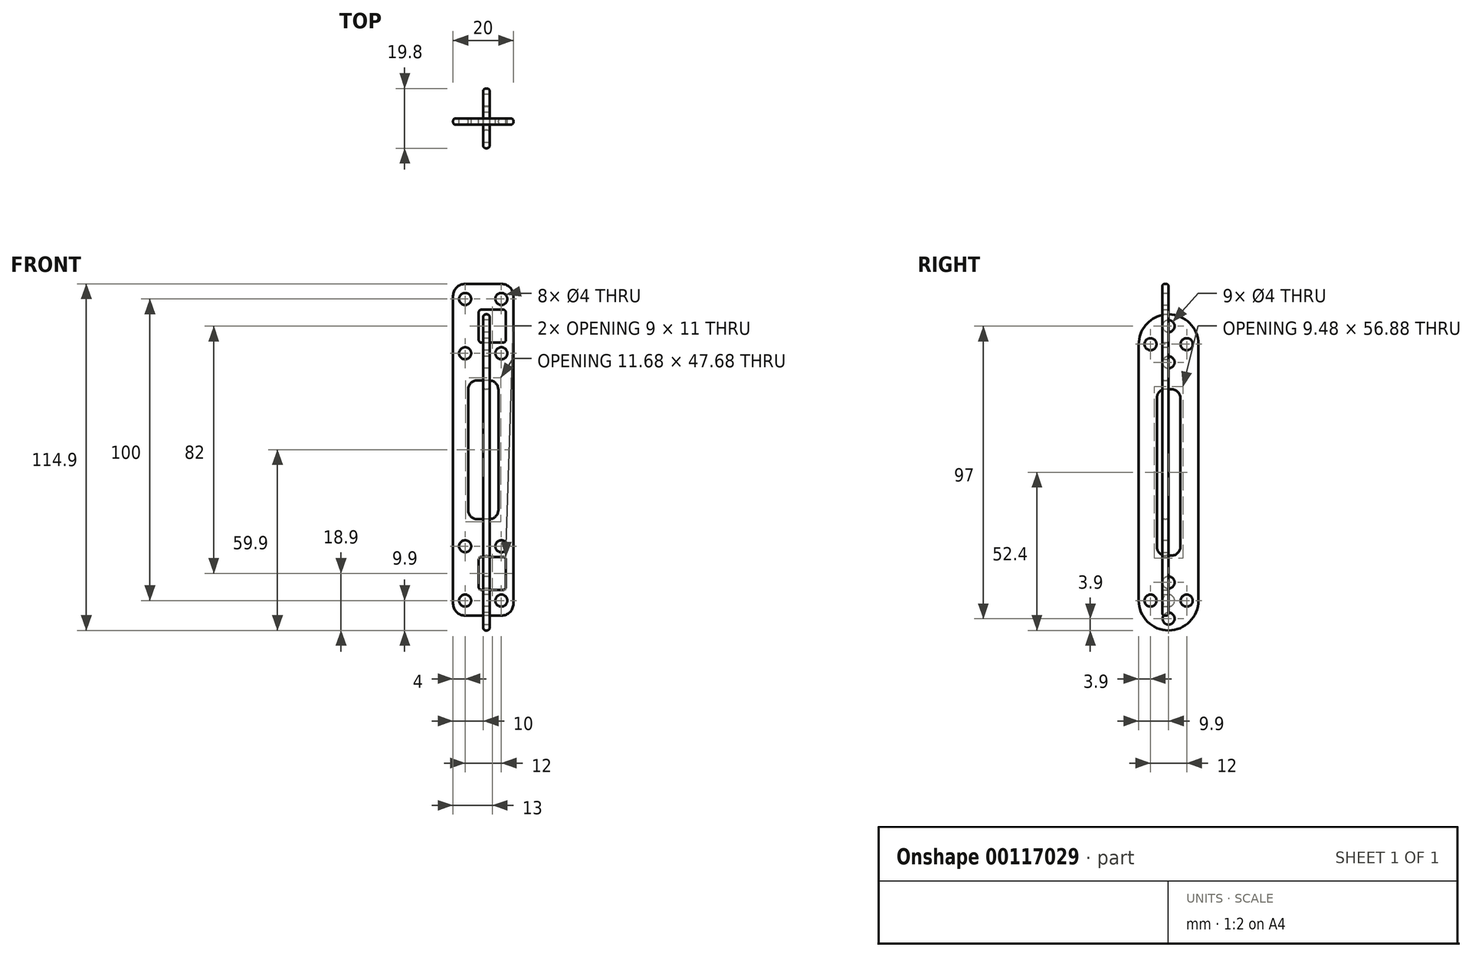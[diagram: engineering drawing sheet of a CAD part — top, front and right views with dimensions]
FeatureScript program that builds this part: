
annotation { "Feature Type Name" : "Feature", "Feature Type Description" : "" }
export const myFeature = defineFeature(function(context is Context, id is Id, definition is map)
    precondition{}
    {
        {
            assignVariable(context, id + "F0", {"name" : "tolerance", "anyValue" : 0.1});
        }
        {
            assignVariable(context, id + "F1", {"name" : "thickness", "anyValue" : 2.2 - getVariable(context, 'tolerance')});
        }
        {
            var Q0;
            Q0=qCreatedBy(makeId("Right.planeOp"),FACE);
            var sketch = newSketch(context, id + "F2", { "sketchPlane" : qUnion([Q0])});
            skLineSegment(sketch, "E0.rect.bottom", {"start": v(12, -9) * mm, "end": v(-12, -9) * mm});
            skLineSegment(sketch, "E0.rect.top", {"start": v(12, 27) * mm, "end": v(-12, 27) * mm});
            skLineSegment(sketch, "E0.rect.left", {"start": v(12, -9) * mm, "end": v(12, 27) * mm});
            skLineSegment(sketch, "E0.rect.right", {"start": v(-12, -9) * mm, "end": v(-12, 27) * mm});
            skPoint(sketch, "E0.rect.middle", {"position": v(0, 9) * mm});
            skCircle(sketch, "E1", {"center": v(0, 0) * mm, "radius": 8.9 * mm});
            skLineSegment(sketch, "E2", {"start": v(0, 27) * mm, "end": v(0, -9) * mm, "construction": true});
            skCircle(sketch, "E3", {"center": v(0, 0) * mm, "radius": 6 * mm, "construction": true});
            skCircle(sketch, "E4", {"center": v(0, -6) * mm, "radius": 2 * mm});
            skCircle(sketch, "E5.1.0", {"center": v(6, 0) * mm, "radius": 2 * mm});
            skCircle(sketch, "E5.2.0", {"center": v(0, 6) * mm, "radius": 2 * mm});
            skCircle(sketch, "E5.3.0", {"center": v(-6, 0) * mm, "radius": 2 * mm});
            skCircle(sketch, "E6", {"center": v(-4.24, 4.24) * mm, "radius": 0.8 * mm});
            skCircle(sketch, "E7.1.0", {"center": v(-4.24, -4.24) * mm, "radius": 0.8 * mm});
            skCircle(sketch, "E7.2.0", {"center": v(4.24, -4.24) * mm, "radius": 0.8 * mm});
            skCircle(sketch, "E7.3.0", {"center": v(4.24, 4.24) * mm, "radius": 0.8 * mm});
            skLineSegment(sketch, "E8", {"start": v(-6, 24) * mm, "end": v(6, 24) * mm, "construction": true});
            skCircle(sketch, "E9", {"center": v(-6, 24) * mm, "radius": 2 * mm});
            skCircle(sketch, "E10", {"center": v(0, 24) * mm, "radius": 2 * mm});
            skCircle(sketch, "E11", {"center": v(6, 24) * mm, "radius": 2 * mm});
            skPoint(sketch, "E12.center", {"position": v(0, 100) * mm});
            skLineSegment(sketch, "E13.rect.right", {"start": v(12, 109) * mm, "end": v(12, 73) * mm});
            skCircle(sketch, "E14", {"center": v(-6, 76) * mm, "radius": 2 * mm});
            skLineSegment(sketch, "E15", {"start": v(0, 73) * mm, "end": v(0, 109) * mm, "construction": true});
            skCircle(sketch, "E16", {"center": v(0, 100) * mm, "radius": 8.9 * mm});
            skLineSegment(sketch, "E13.rect.left", {"start": v(-12, 109) * mm, "end": v(-12, 73) * mm});
            skLineSegment(sketch, "E13.rect.bottom", {"start": v(-12, 109) * mm, "end": v(12, 109) * mm});
            skLineSegment(sketch, "E13.rect.top", {"start": v(-12, 73) * mm, "end": v(12, 73) * mm});
            skLineSegment(sketch, "E17", {"start": v(6, 76) * mm, "end": v(-6, 76) * mm, "construction": true});
            skCircle(sketch, "E18", {"center": v(0, 76) * mm, "radius": 2 * mm});
            skPoint(sketch, "E13.rect.middle", {"position": v(0, 91) * mm});
            skCircle(sketch, "E12.2.0", {"center": v(0, 94) * mm, "radius": 2 * mm});
            skCircle(sketch, "E12.1.0", {"center": v(-6, 100) * mm, "radius": 2 * mm});
            skCircle(sketch, "E19", {"center": v(0, 100) * mm, "radius": 6 * mm, "construction": true});
            skCircle(sketch, "E20", {"center": v(0, 106) * mm, "radius": 2 * mm});
            skCircle(sketch, "E21", {"center": v(-4.24, 104.24) * mm, "radius": 0.8 * mm});
            skCircle(sketch, "E12.3.0", {"center": v(6, 100) * mm, "radius": 2 * mm});
            skCircle(sketch, "E22.3.0", {"center": v(4.24, 104.24) * mm, "radius": 0.8 * mm});
            skCircle(sketch, "E22.2.0", {"center": v(4.24, 95.76) * mm, "radius": 0.8 * mm});
            skCircle(sketch, "E22.1.0", {"center": v(-4.24, 95.76) * mm, "radius": 0.8 * mm});
            skCircle(sketch, "E23", {"center": v(6, 76) * mm, "radius": 2 * mm});
            skSolve(sketch);
        }
        {
            var Q0;
            Q0=qCreatedBy(makeId("Front.planeOp"),FACE);
            var sketch = newSketch(context, id + "F3", { "sketchPlane" : qUnion([Q0])});
            skLineSegment(sketch, "E24", {"start": v(0, 22.5) * mm, "end": v(9, 22.5) * mm});
            skLineSegment(sketch, "E25", {"start": v(9, 22.5) * mm, "end": v(9, 27) * mm});
            skLineSegment(sketch, "E26", {"start": v(9, 27) * mm, "end": v(12, 27) * mm});
            skLineSegment(sketch, "E27", {"start": v(12, 27) * mm, "end": v(12, -9) * mm});
            skLineSegment(sketch, "E28", {"start": v(12, -9) * mm, "end": v(0, -9) * mm});
            skLineSegment(sketch, "E29", {"start": v(12, 8.9) * mm, "end": v(15, 8.9) * mm});
            skLineSegment(sketch, "E30", {"start": v(15, 8.9) * mm, "end": v(15, -8.9) * mm});
            skLineSegment(sketch, "E31", {"start": v(15, -8.9) * mm, "end": v(12, -8.9) * mm});
            skLineSegment(sketch, "E32", {"start": v(0, 1.45) * mm, "end": v(0, -56.88) * mm, "construction": true});
            skLineSegment(sketch, "E33", {"start": v(0, 0) * mm, "end": v(15, 0) * mm, "construction": true});
            skLineSegment(sketch, "E34.MirrorCS", {"start": v(-15, 8.9) * mm, "end": v(-15, -8.9) * mm});
            skLineSegment(sketch, "E35.MirrorCS", {"start": v(0, 22.5) * mm, "end": v(-9, 22.5) * mm});
            skLineSegment(sketch, "E36.MirrorCS", {"start": v(0, 0) * mm, "end": v(-15, 0) * mm, "construction": true});
            skLineSegment(sketch, "E37.MirrorCS", {"start": v(-9, 22.5) * mm, "end": v(-9, 27) * mm});
            skLineSegment(sketch, "E38.MirrorCS", {"start": v(-12, 8.9) * mm, "end": v(-15, 8.9) * mm});
            skLineSegment(sketch, "E39.MirrorCS", {"start": v(-12, -9) * mm, "end": v(0, -9) * mm});
            skLineSegment(sketch, "E40.MirrorCS", {"start": v(-12, 27) * mm, "end": v(-12, -9) * mm});
            skLineSegment(sketch, "E41.MirrorCS", {"start": v(-15, -8.9) * mm, "end": v(-12, -8.9) * mm});
            skLineSegment(sketch, "E42.MirrorCS", {"start": v(-9, 27) * mm, "end": v(-12, 27) * mm});
            skLineSegment(sketch, "E43.MirrorCS", {"start": v(0, 100) * mm, "end": v(-15, 100) * mm, "construction": true});
            skLineSegment(sketch, "E44.MirrorCS", {"start": v(0, 77.5) * mm, "end": v(-9, 77.5) * mm});
            skLineSegment(sketch, "E45", {"start": v(15, 108.9) * mm, "end": v(15, 91.1) * mm});
            skLineSegment(sketch, "E46.MirrorCS", {"start": v(-15, 108.9) * mm, "end": v(-15, 91.1) * mm});
            skLineSegment(sketch, "E47", {"start": v(0, 57.8) * mm, "end": v(0, 0) * mm, "construction": true});
            skLineSegment(sketch, "E48", {"start": v(12, 109) * mm, "end": v(0, 109) * mm});
            skLineSegment(sketch, "E49", {"start": v(12, 109) * mm, "end": v(12, 73) * mm});
            skLineSegment(sketch, "E50", {"start": v(0, 77.5) * mm, "end": v(9, 77.5) * mm});
            skLineSegment(sketch, "E51.MirrorCS", {"start": v(-12, 109) * mm, "end": v(0, 109) * mm});
            skLineSegment(sketch, "E52.MirrorCS", {"start": v(-12, 109) * mm, "end": v(-12, 73) * mm});
            skLineSegment(sketch, "E53", {"start": v(0, 100) * mm, "end": v(15, 100) * mm, "construction": true});
            skLineSegment(sketch, "E54", {"start": v(12, 108.9) * mm, "end": v(15, 108.9) * mm});
            skLineSegment(sketch, "E55", {"start": v(9, 73) * mm, "end": v(12, 73) * mm});
            skLineSegment(sketch, "E56", {"start": v(9, 73) * mm, "end": v(9, 77.5) * mm});
            skLineSegment(sketch, "E57.MirrorCS", {"start": v(-9, 73) * mm, "end": v(-12, 73) * mm});
            skLineSegment(sketch, "E58.MirrorCS", {"start": v(-12, 108.9) * mm, "end": v(-15, 108.9) * mm});
            skLineSegment(sketch, "E59.MirrorCS", {"start": v(-9, 73) * mm, "end": v(-9, 77.5) * mm});
            skLineSegment(sketch, "E60.MirrorCS", {"start": v(-15, 91.1) * mm, "end": v(-12, 91.1) * mm});
            skLineSegment(sketch, "E61", {"start": v(15, 91.1) * mm, "end": v(12, 91.1) * mm});
            skLineSegment(sketch, "E62.bottom", {"start": v(-6, 18) * mm, "end": v(6, 18) * mm, "construction": true});
            skLineSegment(sketch, "E62.top", {"start": v(-6, 0) * mm, "end": v(6, 0) * mm, "construction": true});
            skLineSegment(sketch, "E62.left", {"start": v(-6, 18) * mm, "end": v(-6, 0) * mm, "construction": true});
            skLineSegment(sketch, "E62.right", {"start": v(6, 18) * mm, "end": v(6, 0) * mm, "construction": true});
            skCircle(sketch, "E63", {"center": v(6, 0) * mm, "radius": 2 * mm});
            skCircle(sketch, "E64", {"center": v(-6, 0) * mm, "radius": 2 * mm});
            skCircle(sketch, "E65", {"center": v(-6, 18) * mm, "radius": 2 * mm});
            skCircle(sketch, "E66", {"center": v(6, 18) * mm, "radius": 2 * mm});
            skLineSegment(sketch, "E67.left", {"start": v(-6, 100) * mm, "end": v(-6, 82) * mm, "construction": true});
            skCircle(sketch, "E68", {"center": v(-6, 100) * mm, "radius": 2 * mm});
            skLineSegment(sketch, "E67.right", {"start": v(6, 100) * mm, "end": v(6, 82) * mm, "construction": true});
            skLineSegment(sketch, "E67.bottom", {"start": v(-6, 100) * mm, "end": v(6, 100) * mm, "construction": true});
            skCircle(sketch, "E69", {"center": v(6, 100) * mm, "radius": 2 * mm});
            skCircle(sketch, "E70", {"center": v(6, 82) * mm, "radius": 2 * mm});
            skLineSegment(sketch, "E67.top", {"start": v(-6, 82) * mm, "end": v(6, 82) * mm, "construction": true});
            skCircle(sketch, "E71", {"center": v(-6, 82) * mm, "radius": 2 * mm});
            skLineSegment(sketch, "E72.rect.bottom", {"start": v(7.5, 96.5) * mm, "end": v(-7.5, 96.5) * mm});
            skLineSegment(sketch, "E72.rect.top", {"start": v(7.5, 85.5) * mm, "end": v(-7.5, 85.5) * mm});
            skLineSegment(sketch, "E72.rect.left", {"start": v(7.5, 96.5) * mm, "end": v(7.5, 85.5) * mm});
            skLineSegment(sketch, "E72.rect.right", {"start": v(-7.5, 96.5) * mm, "end": v(-7.5, 85.5) * mm});
            skPoint(sketch, "E72.rect.middle", {"position": v(0, 91) * mm});
            skLineSegment(sketch, "E73.rect.bottom", {"start": v(7.5, 3.5) * mm, "end": v(-7.5, 3.5) * mm});
            skLineSegment(sketch, "E73.rect.top", {"start": v(7.5, 14.5) * mm, "end": v(-7.5, 14.5) * mm});
            skLineSegment(sketch, "E73.rect.left", {"start": v(7.5, 3.5) * mm, "end": v(7.5, 14.5) * mm});
            skLineSegment(sketch, "E73.rect.right", {"start": v(-7.5, 3.5) * mm, "end": v(-7.5, 14.5) * mm});
            skPoint(sketch, "E73.rect.middle", {"position": v(0, 9) * mm});
            skSolve(sketch);
        }
        {
            var Q0;
            Q0=qCreatedBy(makeId("Front.planeOp"),FACE);
            var sketch = newSketch(context, id + "F4", { "sketchPlane" : qUnion([Q0])});
            skLineSegment(sketch, "E74.rect.bottom", {"start": v(6, 105) * mm, "end": v(-6, 105) * mm});
            skLineSegment(sketch, "E74.rect.top", {"start": v(6, -5) * mm, "end": v(-6, -5) * mm});
            skLineSegment(sketch, "E74.rect.left", {"start": v(10, 101) * mm, "end": v(10, -1) * mm});
            skLineSegment(sketch, "E74.rect.right", {"start": v(-10, 101) * mm, "end": v(-10, -1) * mm});
            skPoint(sketch, "E74.rect.middle", {"position": v(0, 50) * mm});
            skCircle(sketch, "E75", {"center": v(-6, 18) * mm, "radius": 2 * mm});
            skCircle(sketch, "E76", {"center": v(6, 18) * mm, "radius": 2 * mm});
            skCircle(sketch, "E77", {"center": v(-6, 0) * mm, "radius": 2 * mm});
            skCircle(sketch, "E78", {"center": v(6, 0) * mm, "radius": 2 * mm});
            skCircle(sketch, "E79", {"center": v(-6, 82) * mm, "radius": 2 * mm});
            skCircle(sketch, "E80", {"center": v(6, 82) * mm, "radius": 2 * mm});
            skCircle(sketch, "E81", {"center": v(-6, 100) * mm, "radius": 2 * mm});
            skCircle(sketch, "E82", {"center": v(6, 100) * mm, "radius": 2 * mm});
            skPoint(sketch, "E83.visualSharp", {"position": v(-10, 105) * mm});
            skArc(sketch, "E83.filletArc", {"start": v(-6, 105) * mm, "mid": v(-8.83, 103.83) * mm, "end": v(-10, 101) * mm});
            skPoint(sketch, "E84.visualSharp", {"position": v(10, 105) * mm});
            skArc(sketch, "E84.filletArc", {"start": v(10, 101) * mm, "mid": v(8.83, 103.83) * mm, "end": v(6, 105) * mm});
            skPoint(sketch, "E85.visualSharp", {"position": v(10, -5) * mm});
            skArc(sketch, "E85.filletArc", {"start": v(6, -5) * mm, "mid": v(8.83, -3.83) * mm, "end": v(10, -1) * mm});
            skPoint(sketch, "E86.visualSharp", {"position": v(-10, -5) * mm});
            skArc(sketch, "E86.filletArc", {"start": v(-10, -1) * mm, "mid": v(-8.83, -3.83) * mm, "end": v(-6, -5) * mm});
            skLineSegment(sketch, "E87.rect.bottom", {"start": v(2, 27) * mm, "end": v(-2, 27) * mm});
            skLineSegment(sketch, "E87.rect.top", {"start": v(2, 73) * mm, "end": v(-2, 73) * mm});
            skLineSegment(sketch, "E87.rect.left", {"start": v(5, 30) * mm, "end": v(5, 70) * mm});
            skLineSegment(sketch, "E87.rect.right", {"start": v(-5, 30) * mm, "end": v(-5, 70) * mm});
            skPoint(sketch, "E88.visualSharp", {"position": v(-5, 73) * mm});
            skArc(sketch, "E88.filletArc", {"start": v(-2, 73) * mm, "mid": v(-4.12, 72.12) * mm, "end": v(-5, 70) * mm});
            skPoint(sketch, "E89.visualSharp", {"position": v(5, 73) * mm});
            skArc(sketch, "E89.filletArc", {"start": v(5, 70) * mm, "mid": v(4.12, 72.12) * mm, "end": v(2, 73) * mm});
            skPoint(sketch, "E90.visualSharp", {"position": v(5, 27) * mm});
            skArc(sketch, "E90.filletArc", {"start": v(2, 27) * mm, "mid": v(4.12, 27.88) * mm, "end": v(5, 30) * mm});
            skPoint(sketch, "E91.visualSharp", {"position": v(-5, 27) * mm});
            skArc(sketch, "E91.filletArc", {"start": v(-5, 30) * mm, "mid": v(-4.12, 27.88) * mm, "end": v(-2, 27) * mm});
            skSolve(sketch);
        }
        {
            var Q0;
            Q0=makeQuery(id+"F4.imprint","IMPRINT",FACE,{"disambiguationData":[TD([[makeQuery(id+"F4.imprint","IMPRINT",EDGE,{"derivedFrom":sQuery(id+"F4.wireOp",EDGE,"E74.rect.bottom")}),1.0]])]});
            extrude(context, id + "F5", {"entities" : qUnion([Q0]), "depth" : (getVariable(context, 'thickness')) * mm});
        }
        {
            var Q0;
            Q0=qCreatedBy(makeId("Front.planeOp"),FACE);
            var sketch = newSketch(context, id + "F6", { "sketchPlane" : qUnion([Q0])});
            skLineSegment(sketch, "E92.rect.bottom", {"start": v(-0.5, 14.5) * mm, "end": v(6.5, 14.5) * mm});
            skLineSegment(sketch, "E92.rect.top", {"start": v(-0.5, 3.5) * mm, "end": v(6.5, 3.5) * mm});
            skLineSegment(sketch, "E92.rect.left", {"start": v(-1.5, 13.5) * mm, "end": v(-1.5, 4.5) * mm});
            skLineSegment(sketch, "E92.rect.right", {"start": v(7.5, 13.5) * mm, "end": v(7.5, 4.5) * mm});
            skPoint(sketch, "E92.rect.middle", {"position": v(3, 9) * mm});
            skPoint(sketch, "E93.visualSharp", {"position": v(-1.5, 14.5) * mm});
            skArc(sketch, "E93.filletArc", {"start": v(-0.5, 14.5) * mm, "mid": v(-1.2, 14.2) * mm, "end": v(-1.5, 13.5) * mm});
            skPoint(sketch, "E94.visualSharp", {"position": v(7.5, 14.5) * mm});
            skArc(sketch, "E94.filletArc", {"start": v(7.5, 13.5) * mm, "mid": v(7.2, 14.2) * mm, "end": v(6.5, 14.5) * mm});
            skPoint(sketch, "E95.visualSharp", {"position": v(7.5, 3.5) * mm});
            skArc(sketch, "E95.filletArc", {"start": v(6.5, 3.5) * mm, "mid": v(7.2, 3.8) * mm, "end": v(7.5, 4.5) * mm});
            skPoint(sketch, "E96.visualSharp", {"position": v(-1.5, 3.5) * mm});
            skArc(sketch, "E96.filletArc", {"start": v(-1.5, 4.5) * mm, "mid": v(-1.2, 3.8) * mm, "end": v(-0.5, 3.5) * mm});
            skPoint(sketch, "E97.visualSharp", {"position": v(7.5, 96.5) * mm});
            skPoint(sketch, "E98.visualSharp", {"position": v(-1.5, 85.5) * mm});
            skPoint(sketch, "E99.rect.middle", {"position": v(3, 91) * mm});
            skPoint(sketch, "E100.visualSharp", {"position": v(7.5, 85.5) * mm});
            skLineSegment(sketch, "E99.rect.top", {"start": v(-0.5, 85.5) * mm, "end": v(6.5, 85.5) * mm});
            skLineSegment(sketch, "E99.rect.right", {"start": v(7.5, 95.5) * mm, "end": v(7.5, 86.5) * mm});
            skPoint(sketch, "E101.visualSharp", {"position": v(-1.5, 96.5) * mm});
            skLineSegment(sketch, "E99.rect.bottom", {"start": v(-0.5, 96.5) * mm, "end": v(6.5, 96.5) * mm});
            skLineSegment(sketch, "E99.rect.left", {"start": v(-1.5, 95.5) * mm, "end": v(-1.5, 86.5) * mm});
            skArc(sketch, "E98.filletArc", {"start": v(-1.5, 86.5) * mm, "mid": v(-1.2, 85.8) * mm, "end": v(-0.5, 85.5) * mm});
            skArc(sketch, "E101.filletArc", {"start": v(-0.5, 96.5) * mm, "mid": v(-1.2, 96.2) * mm, "end": v(-1.5, 95.5) * mm});
            skArc(sketch, "E97.filletArc", {"start": v(7.5, 95.5) * mm, "mid": v(7.2, 96.2) * mm, "end": v(6.5, 96.5) * mm});
            skArc(sketch, "E100.filletArc", {"start": v(6.5, 85.5) * mm, "mid": v(7.2, 85.8) * mm, "end": v(7.5, 86.5) * mm});
            skSolve(sketch);
        }
        {
            var Q0;
            Q0=qSketchRegion(id+"F6",true);
            extrude(context, id + "F7", {"entities" : qUnion([Q0]), "operationType" : NewBodyOperationType.REMOVE, "endBound" : BoundingType.UP_TO_NEXT, "depth" : 25 * mm});
        }
        {
            var Q0;
            Q0=makeQuery(id+"F5.opExtrude","SWEPT_FACE",FACE,{"disambiguationData":[OSD([sQuery(id+"F4.wireOp",EDGE,"E74.rect.left")])]});
            var Q1;
            Q1=makeQuery(id+"F5.opExtrude","SWEPT_FACE",FACE,{"disambiguationData":[OSD([sQuery(id+"F4.wireOp",EDGE,"E87.rect.right")])]});
            fillet(context, id + "F8", {"entities" : qUnion([Q0, Q1]), "radius" : (getVariable(context, 'thickness') / 2.5) * mm, "tangentPropagation" : true, "allowEdgeOverflow" : false});
        }
        {
            var Q0;
            Q0=qCreatedBy(makeId("Right.planeOp"),FACE);
            var sketch = newSketch(context, id + "F9", { "sketchPlane" : qUnion([Q0])});
            skCircle(sketch, "E102", {"center": v(0, 0) * mm, "radius": 9.9 * mm});
            skLineSegment(sketch, "E103", {"start": v(9.9, 0) * mm, "end": v(9.9, 85) * mm});
            skLineSegment(sketch, "E104", {"start": v(-9.9, 85) * mm, "end": v(-9.9, 0) * mm});
            skCircle(sketch, "E105", {"center": v(-6, 0) * mm, "radius": 2 * mm});
            skCircle(sketch, "E106", {"center": v(0, 6) * mm, "radius": 2 * mm});
            skCircle(sketch, "E107", {"center": v(6, 0) * mm, "radius": 2 * mm});
            skCircle(sketch, "E108", {"center": v(0, -6) * mm, "radius": 2 * mm});
            skCircle(sketch, "E109", {"center": v(0, 0) * mm, "radius": 2 * mm});
            skLineSegment(sketch, "E110.rect.bottom", {"start": v(0.9, 14.9) * mm, "end": v(-0.9, 14.9) * mm});
            skLineSegment(sketch, "E110.rect.top", {"start": v(0.9, 70.1) * mm, "end": v(-0.9, 70.1) * mm});
            skLineSegment(sketch, "E110.rect.left", {"start": v(3.9, 17.9) * mm, "end": v(3.9, 67.1) * mm});
            skLineSegment(sketch, "E110.rect.right", {"start": v(-3.9, 17.9) * mm, "end": v(-3.9, 67.1) * mm});
            skPoint(sketch, "E110.rect.middle", {"position": v(0, 42.5) * mm});
            skPoint(sketch, "E111.visualSharp", {"position": v(-3.9, 14.9) * mm});
            skArc(sketch, "E111.filletArc", {"start": v(-3.9, 17.9) * mm, "mid": v(-3.02, 15.78) * mm, "end": v(-0.9, 14.9) * mm});
            skPoint(sketch, "E112.visualSharp", {"position": v(3.9, 14.9) * mm});
            skArc(sketch, "E112.filletArc", {"start": v(0.9, 14.9) * mm, "mid": v(3.02, 15.78) * mm, "end": v(3.9, 17.9) * mm});
            skPoint(sketch, "E113.visualSharp", {"position": v(-3.9, 70.1) * mm});
            skArc(sketch, "E113.filletArc", {"start": v(-0.9, 70.1) * mm, "mid": v(-3.02, 69.22) * mm, "end": v(-3.9, 67.1) * mm});
            skPoint(sketch, "E114.visualSharp", {"position": v(3.9, 70.1) * mm});
            skArc(sketch, "E114.filletArc", {"start": v(3.9, 67.1) * mm, "mid": v(3.02, 69.22) * mm, "end": v(0.9, 70.1) * mm});
            skCircle(sketch, "E115", {"center": v(0, 85) * mm, "radius": 9.9 * mm});
            skCircle(sketch, "E116", {"center": v(0, 85) * mm, "radius": 6 * mm, "construction": true});
            skCircle(sketch, "E117", {"center": v(0, 91) * mm, "radius": 2 * mm});
            skCircle(sketch, "E118.1.0", {"center": v(-6, 85) * mm, "radius": 2 * mm});
            skCircle(sketch, "E118.2.0", {"center": v(0, 79) * mm, "radius": 2 * mm});
            skCircle(sketch, "E118.3.0", {"center": v(6, 85) * mm, "radius": 2 * mm});
            skSolve(sketch);
        }
        {
            var Q0;
            Q0=qSketchRegion(id+"F9",true);
            extrude(context, id + "F10", {"entities" : qUnion([Q0]), "depth" : (getVariable(context, 'thickness')) * mm});
        }
        {
            var Q0;
            Q0=makeQuery(id+"F10.opExtrude","SWEPT_FACE",FACE,{"disambiguationData":[OSD([sQuery(id+"F9.wireOp",EDGE,"E103")])]});
            var Q1;
            Q1=makeQuery(id+"F10.opExtrude","SWEPT_FACE",FACE,{"disambiguationData":[OSD([sQuery(id+"F9.wireOp",EDGE,"E110.rect.right")])]});
            fillet(context, id + "F11", {"entities" : qUnion([Q0, Q1]), "radius" : (getVariable(context, 'thickness') / 2.5) * mm, "tangentPropagation" : true, "allowEdgeOverflow" : false});
        }
    });
